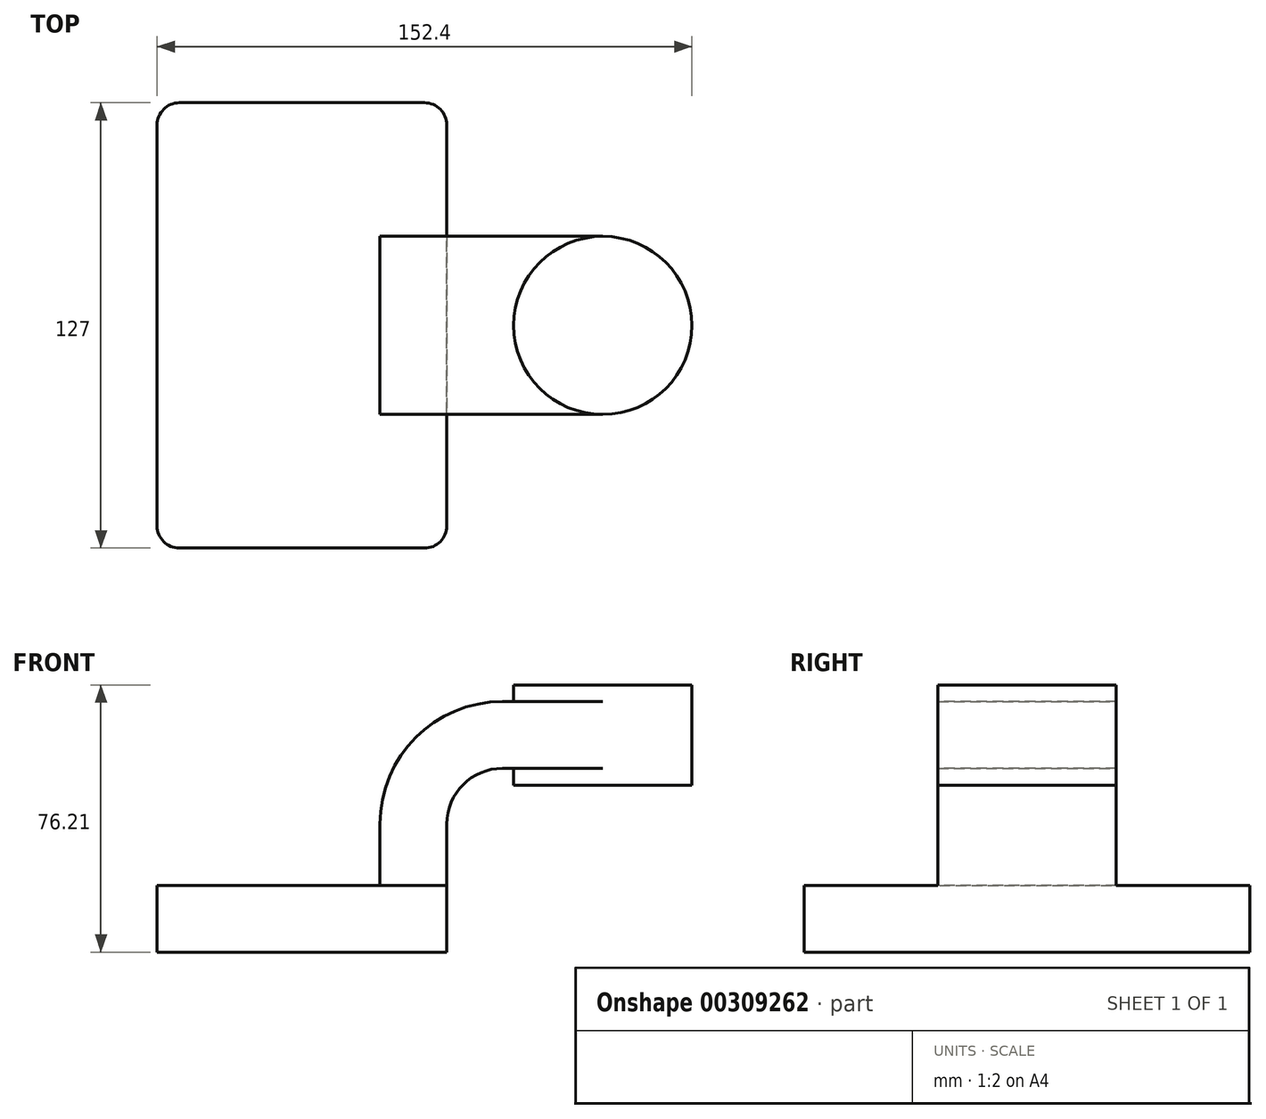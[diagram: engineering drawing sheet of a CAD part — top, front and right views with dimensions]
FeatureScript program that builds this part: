
annotation { "Feature Type Name" : "Feature", "Feature Type Description" : "" }
export const myFeature = defineFeature(function(context is Context, id is Id, definition is map)
    precondition{}
    {
        {
            var Q0;
            Q0=qCreatedBy(makeId("Front.planeOp"),FACE);
            var sketch = newSketch(context, id + "F0", { "sketchPlane" : qUnion([Q0])});
            skLineSegment(sketch, "E0.bottom", {"start": v(-41.28, 9.52) * mm, "end": v(41.28, 9.53) * mm});
            skLineSegment(sketch, "E0.top", {"start": v(-41.28, -9.53) * mm, "end": v(41.28, -9.52) * mm});
            skLineSegment(sketch, "E0.left", {"start": v(-41.28, 9.52) * mm, "end": v(-41.28, -9.53) * mm});
            skLineSegment(sketch, "E0.right", {"start": v(41.28, 9.53) * mm, "end": v(41.28, -9.52) * mm});
            skPoint(sketch, "E0.middle", {"position": v(0, 0) * mm});
            skLineSegment(sketch, "E1.bottom", {"start": v(111.13, 38.1) * mm, "end": v(60.33, 38.1) * mm});
            skLineSegment(sketch, "E1.top", {"start": v(111.13, 66.68) * mm, "end": v(60.33, 66.68) * mm});
            skLineSegment(sketch, "E1.left", {"start": v(111.13, 38.1) * mm, "end": v(111.13, 66.67) * mm});
            skLineSegment(sketch, "E1.right", {"start": v(60.33, 38.1) * mm, "end": v(60.33, 66.67) * mm});
            skPoint(sketch, "E1.middle", {"position": v(85.72, 52.39) * mm});
            skLineSegment(sketch, "E2", {"start": v(41.28, 9.53) * mm, "end": v(41.28, 27) * mm});
            skArc(sketch, "E3", {"start": v(41.28, 27) * mm, "mid": v(45.92, 38.23) * mm, "end": v(57.15, 42.88) * mm});
            skLineSegment(sketch, "E4", {"start": v(57.15, 42.88) * mm, "end": v(85.72, 42.88) * mm});
            skLineSegment(sketch, "E5.0", {"start": v(57.15, 61.93) * mm, "end": v(85.72, 61.93) * mm});
            skArc(sketch, "E5.1", {"start": v(22.23, 27) * mm, "mid": v(32.45, 51.7) * mm, "end": v(57.15, 61.93) * mm});
            skLineSegment(sketch, "E5.2", {"start": v(22.23, 9.53) * mm, "end": v(22.23, 27) * mm});
            skFitSpline(sketch, "E6", {"points": [v(57.15, 61.93) * mm, v(-41.28, 9.52) * mm], "startDerivative": vector(-171.45, 3.82) * mm, "endDerivative": vector(0.88, -48.96) * mm});
            skLineSegment(sketch, "E7", {"start": v(85.72, 61.93) * mm, "end": v(85.72, 42.88) * mm});
            skLineSegment(sketch, "E8", {"start": v(85.72, 61.93) * mm, "end": v(85.72, 66.68) * mm});
            skLineSegment(sketch, "E9", {"start": v(85.72, 66.68) * mm, "end": v(85.72, 38.1) * mm});
            skSolve(sketch);
        }
        {
            var Q0;
            Q0=makeQuery(id+"F0.imprint","IMPRINT",FACE,{"disambiguationData":[TD([[makeQuery(id+"F0.imprint","IMPRINT",EDGE,{"derivedFrom":sQuery(id+"F0.wireOp",EDGE,"E0.top")}),1.0]])]});
            extrude(context, id + "F1", {"entities" : qUnion([Q0]), "endBound" : BoundingType.SYMMETRIC, "depth" : 127 * mm});
        }
        {
            var Q0;
            {var subQ1=sQuery(id+"F0.wireOp",EDGE,"E2");Q0=makeQuery(id+"F0.imprint","IMPRINT",FACE,{"disambiguationData":[TD([[makeQuery(id+"F0.imprint","IMPRINT",EDGE,{"derivedFrom":subQ1}),1.0]])]});}
            var Q1;
            {var subQ0=sQuery(id+"F0.wireOp",EDGE,"E4");var subQ1=sQuery(id+"F0.wireOp",EDGE,"E1.right");var subQ2=makeQuery(id+"F0.imprint","INTERSECT",VERTEX,{"derivedFrom":[subQ1,subQ0]});Q1=makeQuery(id+"F0.imprint","IMPRINT",FACE,{"disambiguationData":[TD([[makeQuery(id+"F0.imprint","IMPRINT",EDGE,{"disambiguationData":[TD([[subQ2,-1.0]])],"derivedFrom":subQ1}),-1.0]])]});}
            extrude(context, id + "F2", {"entities" : qUnion([Q0, Q1]), "operationType" : NewBodyOperationType.ADD, "endBound" : BoundingType.SYMMETRIC, "oppositeDirection" : true, "depth" : 50.8 * mm});
        }
        {
            var Q0;
            Q0=makeQuery(id+"F0.imprint","IMPRINT",FACE,{"disambiguationData":[TD([[makeQuery(id+"F0.imprint","IMPRINT",EDGE,{"derivedFrom":sQuery(id+"F0.wireOp",EDGE,"E5.1")}),1.0]])]});
            extrude(context, id + "F3", {"entities" : qUnion([Q0]), "operationType" : NewBodyOperationType.ADD, "endBound" : BoundingType.SYMMETRIC, "depth" : 15.88 * mm});
        }
        {
            var Q0;
            {var subQ0=sQuery(id+"F0.wireOp",EDGE,"E1.left");Q0=makeQuery(id+"F0.imprint","IMPRINT",FACE,{"disambiguationData":[TD([[makeQuery(id+"F0.imprint","IMPRINT",EDGE,{"derivedFrom":subQ0}),1.0]])]});}
            var Q1;
            Q1=sQuery(id+"F0.wireOp",EDGE,"E9");
            revolve(context, id + "F4", {"operationType" : NewBodyOperationType.ADD, "entities" : qUnion([Q0]), "axis" : qUnion([Q1]), "revolveType" : RevolveType.FULL});
        }
        {
            var Q0;
            Q0=makeQuery(id+"F1.opExtrude","CAP_EDGE",EDGE,{"disambiguationData":[OSD([sQuery(id+"F0.wireOp",EDGE,"E0.right")])],"isStart":false});
            var Q1;
            Q1=makeQuery(id+"F1.opExtrude","CAP_EDGE",EDGE,{"disambiguationData":[OSD([sQuery(id+"F0.wireOp",EDGE,"E0.right")])],"isStart":true});
            var Q2;
            Q2=makeQuery(id+"F1.opExtrude","CAP_EDGE",EDGE,{"disambiguationData":[OSD([sQuery(id+"F0.wireOp",EDGE,"E0.left")])],"isStart":false});
            var Q3;
            Q3=makeQuery(id+"F1.opExtrude","CAP_EDGE",EDGE,{"disambiguationData":[OSD([sQuery(id+"F0.wireOp",EDGE,"E0.left")])],"isStart":true});
            fillet(context, id + "F5", {"entities" : qUnion([Q0, Q1, Q2, Q3]), "radius" : 6.35 * mm, "tangentPropagation" : true, "allowEdgeOverflow" : false});
        }
    });
